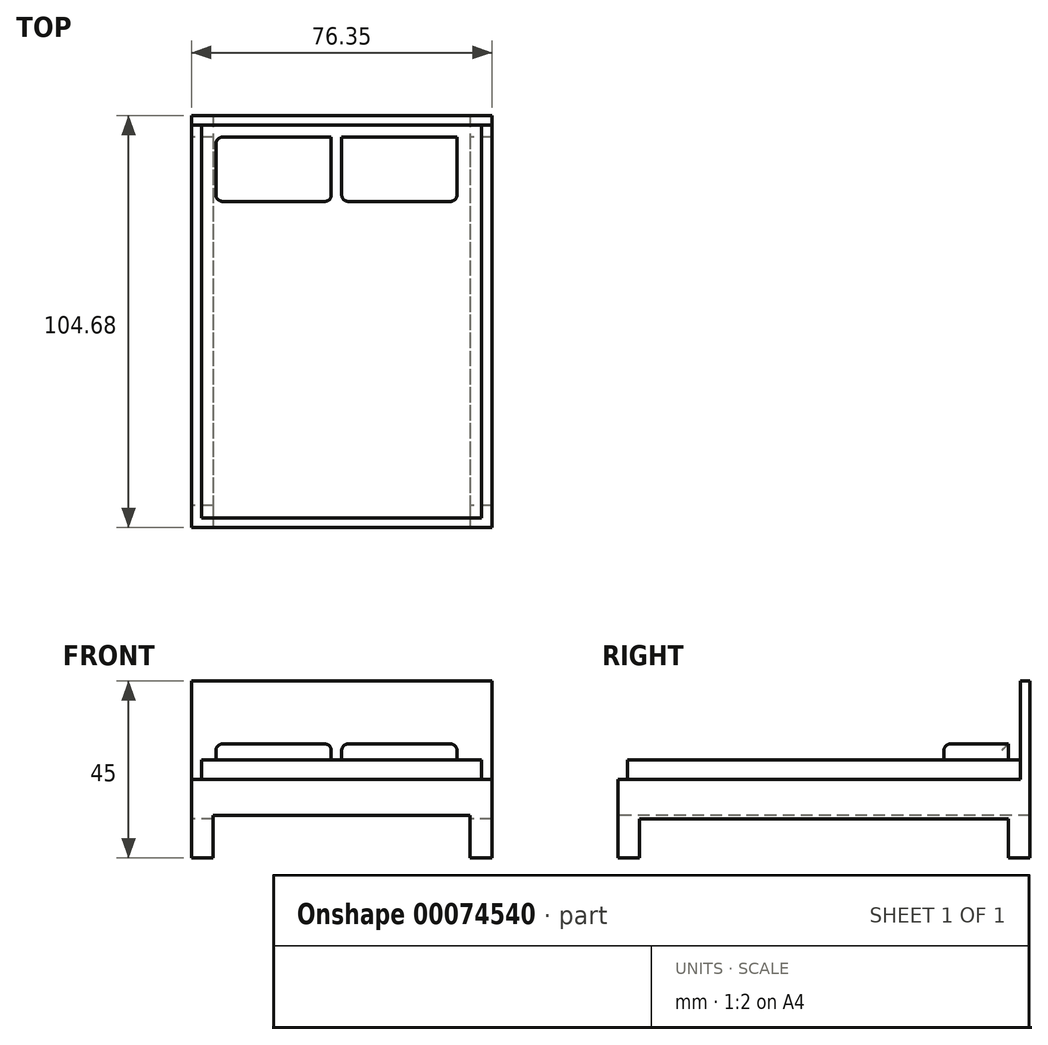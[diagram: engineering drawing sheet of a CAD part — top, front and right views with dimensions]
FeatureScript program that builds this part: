
annotation { "Feature Type Name" : "Feature", "Feature Type Description" : "" }
export const myFeature = defineFeature(function(context is Context, id is Id, definition is map)
    precondition{}
    {
        {
            var Q0;
            Q0=qCreatedBy(makeId("Top.planeOp"),FACE);
            var sketch = newSketch(context, id + "F0", { "sketchPlane" : qUnion([Q0])});
            skLineSegment(sketch, "E0.bottom", {"start": v(-38.41, 70.83) * mm, "end": v(37.94, 70.83) * mm});
            skLineSegment(sketch, "E0.top", {"start": v(-38.41, -33.85) * mm, "end": v(37.94, -33.85) * mm});
            skLineSegment(sketch, "E0.left", {"start": v(-38.41, 70.83) * mm, "end": v(-38.41, -33.85) * mm});
            skLineSegment(sketch, "E0.right", {"start": v(37.94, 70.83) * mm, "end": v(37.94, -33.85) * mm});
            skLineSegment(sketch, "E1", {"start": v(0, -33.85) * mm, "end": v(37.94, -33.85) * mm, "construction": true});
            skSolve(sketch);
        }
        {
            var Q0;
            Q0 = qSketchRegion(id + "F0", true);
            extrude(context, id + "F1", {"entities" : qUnion([Q0]), "depth" : 20 * mm});
        }
        {
            var Q0;
            Q0=makeQuery(id+"F1.opExtrude","SWEPT_FACE",FACE,{"disambiguationData":[OSD([sQuery(id+"F0.wireOp",EDGE,"E0.top")])]});
            var sketch = newSketch(context, id + "F2", { "sketchPlane" : qUnion([Q0])});
            skLineSegment(sketch, "E2.bottom", {"start": v(-32.9, 10.8) * mm, "end": v(32.41, 10.8) * mm});
            skLineSegment(sketch, "E2.top", {"start": v(-32.9, 0) * mm, "end": v(32.41, 0) * mm});
            skLineSegment(sketch, "E2.left", {"start": v(-32.9, 10.8) * mm, "end": v(-32.9, 0) * mm});
            skLineSegment(sketch, "E2.right", {"start": v(32.41, 10.8) * mm, "end": v(32.41, 0) * mm});
            skLineSegment(sketch, "E3", {"start": v(-38.41, 9.37) * mm, "end": v(-32.9, 9.37) * mm});
            skLineSegment(sketch, "E4", {"start": v(32.41, 9.37) * mm, "end": v(37.94, 9.37) * mm});
            skPoint(sketch, "E4.startSnap0", {"position": v(32.41, 5.4) * mm});
            skSolve(sketch);
        }
        {
            var Q0;
            Q0 = qSketchRegion(id + "F2", true);
            var Q1;
            {var subQ4=sQuery(id+"F2.wireOp",EDGE,"E2.bottom");Q1=makeQuery(id+"F2.imprint","IMPRINT",FACE,{"disambiguationData":[TD([[makeQuery(id+"F2.imprint","IMPRINT",EDGE,{"derivedFrom":subQ4}),-1.0]])]});}
            extrude(context, id + "F3", {"entities" : qUnion([Q0, Q1]), "operationType" : NewBodyOperationType.REMOVE, "oppositeDirection" : true, "depth" : 105 * mm});
        }
        {
            var Q0;
            Q0=makeQuery(id+"F1.opExtrude","SWEPT_FACE",FACE,{"disambiguationData":[OSD([sQuery(id+"F0.wireOp",EDGE,"E0.left")])]});
            var sketch = newSketch(context, id + "F4", { "sketchPlane" : qUnion([Q0])});
            skPoint(sketch, "E5.firstSnap0", {"position": v(-70.83, 10) * mm});
            skLineSegment(sketch, "E5.bottom", {"start": v(-65.3, 10) * mm, "end": v(28.33, 10) * mm});
            skLineSegment(sketch, "E5.top", {"start": v(-65.3, 0) * mm, "end": v(28.33, 0) * mm});
            skLineSegment(sketch, "E5.left", {"start": v(-65.3, 10) * mm, "end": v(-65.3, 0) * mm});
            skLineSegment(sketch, "E5.right", {"start": v(28.33, 10) * mm, "end": v(28.33, 0) * mm});
            skLineSegment(sketch, "E6", {"start": v(28.33, 10) * mm, "end": v(33.85, 10) * mm});
            skLineSegment(sketch, "E7", {"start": v(33.85, 10) * mm, "end": v(28.33, 10) * mm});
            skLineSegment(sketch, "E8", {"start": v(-65.3, 10) * mm, "end": v(-70.83, 10) * mm});
            skSolve(sketch);
        }
        {
            var Q0;
            Q0=makeQuery(id+"F4.imprint","IMPRINT",FACE,{"disambiguationData":[TD([[makeQuery(id+"F4.imprint","IMPRINT",EDGE,{"derivedFrom":sQuery(id+"F4.wireOp",EDGE,"E5.bottom")}),-1.0]])]});
            extrude(context, id + "F5", {"entities" : qUnion([Q0]), "operationType" : NewBodyOperationType.REMOVE, "oppositeDirection" : true, "depth" : 100 * mm});
        }
        {
            var Q0;
            Q0=makeQuery(id+"F1.opExtrude","CAP_FACE",FACE,{"disambiguationData":[OSD([sQuery(id+"F0.wireOp",EDGE,"E0.bottom"),sQuery(id+"F0.wireOp",EDGE,"E0.top"),sQuery(id+"F0.wireOp",EDGE,"E0.left"),sQuery(id+"F0.wireOp",EDGE,"E0.right")])],"isStart":false});
            var sketch = newSketch(context, id + "F6", { "sketchPlane" : qUnion([Q0])});
            skLineSegment(sketch, "E9.bottom", {"start": v(-35.77, 68.43) * mm, "end": v(35.3, 68.43) * mm});
            skLineSegment(sketch, "E9.top", {"start": v(-35.77, -31.45) * mm, "end": v(35.3, -31.45) * mm});
            skLineSegment(sketch, "E9.left", {"start": v(-35.77, 68.43) * mm, "end": v(-35.77, -31.45) * mm});
            skLineSegment(sketch, "E9.right", {"start": v(35.3, 68.43) * mm, "end": v(35.3, -31.45) * mm});
            skLineSegment(sketch, "E10", {"start": v(-38.41, 38.41) * mm, "end": v(-35.77, 38.41) * mm, "construction": true});
            skLineSegment(sketch, "E11", {"start": v(35.3, 37.04) * mm, "end": v(37.94, 37.04) * mm, "construction": true});
            skLineSegment(sketch, "E12", {"start": v(0, 70.83) * mm, "end": v(-0.24, 68.43) * mm, "construction": true});
            skPoint(sketch, "E12.startSnap0", {"position": v(-0.24, 70.83) * mm});
            skLineSegment(sketch, "E13", {"start": v(-0.24, 68.43) * mm, "end": v(-0.24, 70.83) * mm, "construction": true});
            skLineSegment(sketch, "E14", {"start": v(-0.24, -31.45) * mm, "end": v(-0.24, -33.85) * mm, "construction": true});
            skLineSegment(sketch, "E15", {"start": v(-35.77, 68.43) * mm, "end": v(-38.41, 68.43) * mm});
            skLineSegment(sketch, "E16", {"start": v(-38.41, 68.43) * mm, "end": v(-35.77, 68.43) * mm});
            skLineSegment(sketch, "E17", {"start": v(35.3, 68.43) * mm, "end": v(37.94, 68.43) * mm});
            skSolve(sketch);
        }
        {
            var Q0;
            Q0=makeQuery(id+"F6.imprint","IMPRINT",FACE,{"disambiguationData":[TD([[makeQuery(id+"F6.imprint","IMPRINT",EDGE,{"derivedFrom":sQuery(id+"F6.wireOp",EDGE,"E9.bottom")}),1.0]])]});
            extrude(context, id + "F7", {"entities" : qUnion([Q0]), "operationType" : NewBodyOperationType.ADD, "depth" : 25 * mm});
        }
        {
            var Q0;
            Q0=makeQuery(id+"F6.imprint","IMPRINT",FACE,{"disambiguationData":[TD([[makeQuery(id+"F6.imprint","IMPRINT",EDGE,{"derivedFrom":sQuery(id+"F6.wireOp",EDGE,"E9.bottom")}),-1.0]])]});
            extrude(context, id + "F8", {"entities" : qUnion([Q0]), "operationType" : NewBodyOperationType.ADD, "depth" : 5 * mm});
        }
        {
            var Q0;
            Q0=makeQuery(id+"F8.opExtrude","CAP_FACE",FACE,{"disambiguationData":[OSD([sQuery(id+"F6.wireOp",EDGE,"E9.bottom"),sQuery(id+"F6.wireOp",EDGE,"E9.top"),sQuery(id+"F6.wireOp",EDGE,"E9.left"),sQuery(id+"F6.wireOp",EDGE,"E9.right")])],"isStart":false});
            var sketch = newSketch(context, id + "F9", { "sketchPlane" : qUnion([Q0])});
            skLineSegment(sketch, "E18.bottom", {"start": v(-32.17, 65.3) * mm, "end": v(-2.88, 65.3) * mm});
            skLineSegment(sketch, "E18.top", {"start": v(-32.17, 48.98) * mm, "end": v(-2.88, 48.98) * mm});
            skLineSegment(sketch, "E18.left", {"start": v(-32.17, 65.3) * mm, "end": v(-32.17, 48.98) * mm});
            skLineSegment(sketch, "E18.right", {"start": v(-2.88, 65.3) * mm, "end": v(-2.88, 48.98) * mm});
            skPoint(sketch, "E19.firstSnap0", {"position": v(-0.24, 68.43) * mm});
            skLineSegment(sketch, "E19.bottom", {"start": v(-0.24, 65.3) * mm, "end": v(29.05, 65.3) * mm});
            skLineSegment(sketch, "E19.top", {"start": v(-0.24, 48.98) * mm, "end": v(29.05, 48.98) * mm});
            skLineSegment(sketch, "E19.left", {"start": v(-0.24, 65.3) * mm, "end": v(-0.24, 48.98) * mm});
            skLineSegment(sketch, "E19.right", {"start": v(29.05, 65.3) * mm, "end": v(29.05, 48.98) * mm});
            skSolve(sketch);
        }
        {
            var Q0;
            Q0=makeQuery(id+"F9.imprint","IMPRINT",FACE,{"disambiguationData":[TD([[makeQuery(id+"F9.imprint","IMPRINT",EDGE,{"derivedFrom":sQuery(id+"F9.wireOp",EDGE,"E18.bottom")}),-1.0]])]});
            var Q1;
            Q1=makeQuery(id+"F9.imprint","IMPRINT",FACE,{"disambiguationData":[TD([[makeQuery(id+"F9.imprint","IMPRINT",EDGE,{"derivedFrom":sQuery(id+"F9.wireOp",EDGE,"E19.bottom")}),-1.0]])]});
            extrude(context, id + "F10", {"entities" : qUnion([Q0, Q1]), "operationType" : NewBodyOperationType.ADD, "depth" : 4 * mm});
        }
        {
            var Q0;
            Q0=makeQuery(id+"F10.opExtrude","CAP_EDGE",EDGE,{"disambiguationData":[OSD([sQuery(id+"F9.wireOp",EDGE,"E18.top")])],"isStart":false});
            var Q1;
            Q1=makeQuery(id+"F10.opExtrude","SWEPT_EDGE",EDGE,{"disambiguationData":[OSD([sQuery(id+"F9.wireOp",EDGE,"E18.bottom"),sQuery(id+"F9.wireOp",EDGE,"E18.left")])]});
            var Q2;
            Q2=makeQuery(id+"F10.opExtrude","SWEPT_EDGE",EDGE,{"disambiguationData":[OSD([sQuery(id+"F9.wireOp",EDGE,"E19.top"),sQuery(id+"F9.wireOp",EDGE,"E19.left")])]});
            var Q3;
            Q3=makeQuery(id+"F10.opExtrude","CAP_EDGE",EDGE,{"disambiguationData":[OSD([sQuery(id+"F9.wireOp",EDGE,"E19.top")])],"isStart":false});
            var Q4;
            Q4=makeQuery(id+"F10.opExtrude","CAP_EDGE",EDGE,{"disambiguationData":[OSD([sQuery(id+"F9.wireOp",EDGE,"E19.left")])],"isStart":false});
            var Q5;
            Q5=makeQuery(id+"F10.opExtrude","CAP_EDGE",EDGE,{"disambiguationData":[OSD([sQuery(id+"F9.wireOp",EDGE,"E18.left")])],"isStart":false});
            var Q6;
            Q6=makeQuery(id+"F10.opExtrude","SWEPT_EDGE",EDGE,{"disambiguationData":[OSD([sQuery(id+"F9.wireOp",EDGE,"E18.top"),sQuery(id+"F9.wireOp",EDGE,"E18.left")])]});
            var Q7;
            Q7=makeQuery(id+"F10.opExtrude","SWEPT_EDGE",EDGE,{"disambiguationData":[OSD([sQuery(id+"F9.wireOp",EDGE,"E18.top"),sQuery(id+"F9.wireOp",EDGE,"E18.right")])]});
            var Q8;
            Q8=makeQuery(id+"F10.opExtrude","CAP_EDGE",EDGE,{"disambiguationData":[OSD([sQuery(id+"F9.wireOp",EDGE,"E18.right")])],"isStart":false});
            var Q9;
            Q9=makeQuery(id+"F10.opExtrude","CAP_EDGE",EDGE,{"disambiguationData":[OSD([sQuery(id+"F9.wireOp",EDGE,"E19.right")])],"isStart":false});
            var Q10;
            Q10=makeQuery(id+"F10.opExtrude","SWEPT_EDGE",EDGE,{"disambiguationData":[OSD([sQuery(id+"F9.wireOp",EDGE,"E19.top"),sQuery(id+"F9.wireOp",EDGE,"E19.right")])]});
            fillet(context, id + "F11", {"entities" : qUnion([Q0, Q1, Q2, Q3, Q4, Q5, Q6, Q7, Q8, Q9, Q10]), "radius" : 1.65 * mm, "tangentPropagation" : true, "allowEdgeOverflow" : false});
        }
    });
